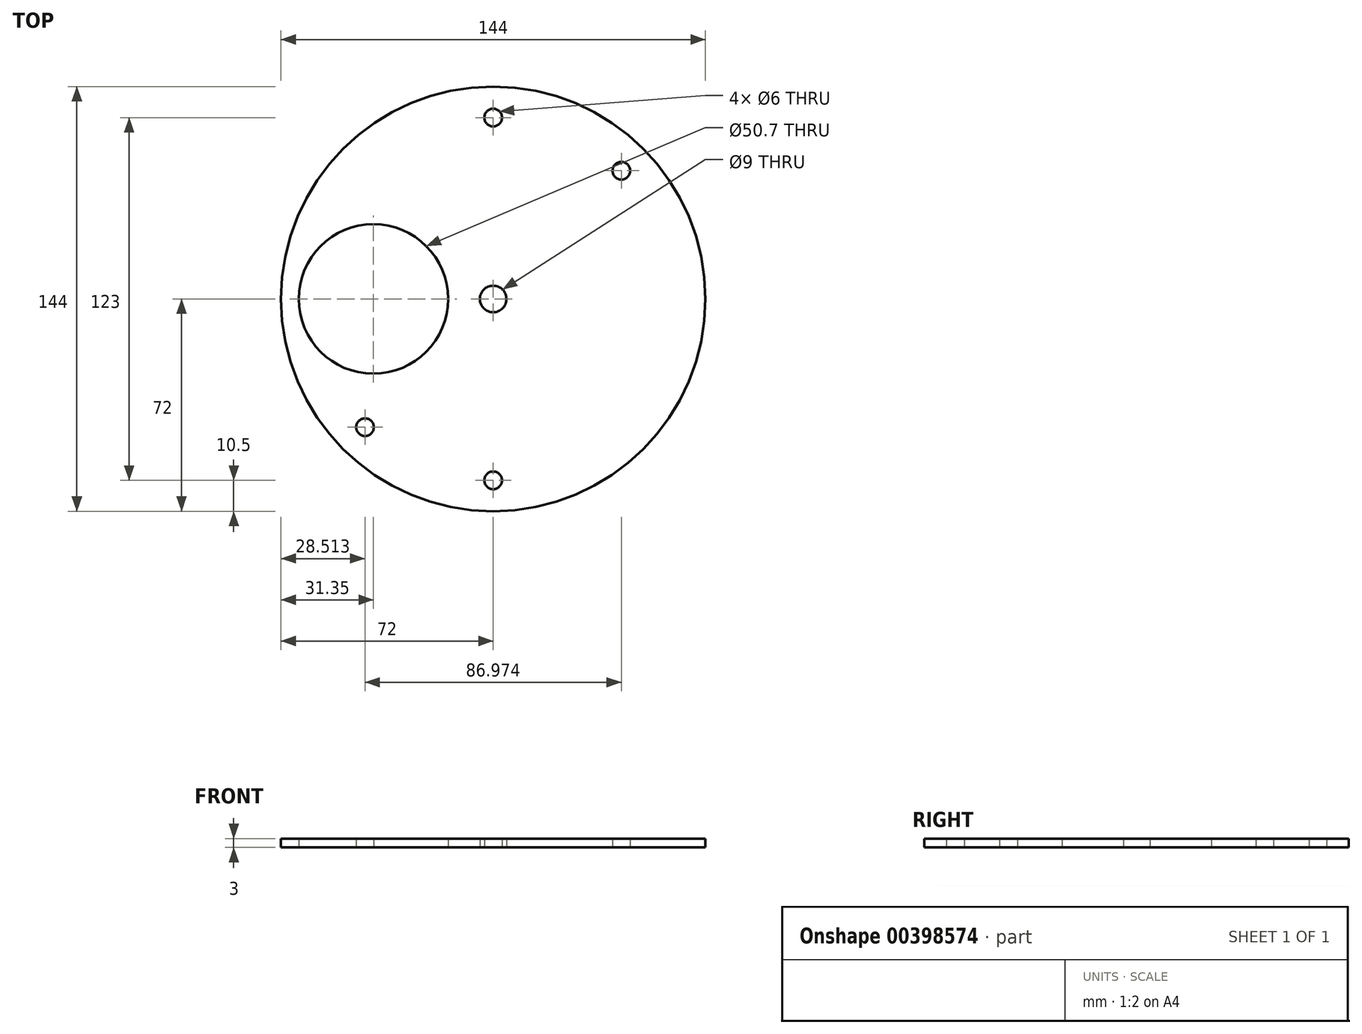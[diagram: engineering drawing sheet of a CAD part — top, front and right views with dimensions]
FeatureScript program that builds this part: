
annotation { "Feature Type Name" : "Feature", "Feature Type Description" : "" }
export const myFeature = defineFeature(function(context is Context, id is Id, definition is map)
    precondition{}
    {
        {
            var Q0;
            Q0=qCreatedBy(makeId("Top.planeOp"),FACE);
            var sketch = newSketch(context, id + "F0", { "sketchPlane" : qUnion([Q0])});
            skCircle(sketch, "E0", {"center": v(0, 0) * mm, "radius": 72 * mm});
            skCircle(sketch, "E1", {"center": v(-40.65, 0) * mm, "radius": 25.35 * mm});
            skCircle(sketch, "E2", {"center": v(0, 61.5) * mm, "radius": 3 * mm});
            skCircle(sketch, "E3.MirrorC", {"center": v(0, -61.5) * mm, "radius": 3 * mm});
            skCircle(sketch, "E4", {"center": v(43.49, 43.49) * mm, "radius": 3 * mm});
            skCircle(sketch, "E5", {"center": v(-43.49, -43.49) * mm, "radius": 3 * mm});
            skCircle(sketch, "E6", {"center": v(0, 0) * mm, "radius": 4.5 * mm});
            skSolve(sketch);
        }
        {
            var Q0;
            Q0=makeQuery(id+"F0.imprint","IMPRINT",FACE,{"disambiguationData":[TD([[makeQuery(id+"F0.imprint","IMPRINT",EDGE,{"derivedFrom":sQuery(id+"F0.wireOp",EDGE,"E0")}),1.0]])]});
            extrude(context, id + "F1", {"entities" : qUnion([Q0]), "depth" : 3 * mm});
        }
    });
